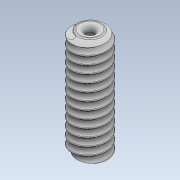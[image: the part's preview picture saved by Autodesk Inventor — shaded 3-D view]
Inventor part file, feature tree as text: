
AUTODESK INVENTOR PART (.ipt)
format: ipt  version: 2022 (Build 260153000, 153)  size: 748,032 bytes
history: native  units: in
note: dims shown in document units (in); Inventor stores cm internally (conversion verified against a paired STEP export)
features: sketch x7, revolve x4, extrude x3, fillet x3, thread x1, helix x1, other x1
ambient origin geometry x8: Origin, YZ Plane, XZ Plane, XY Plane, X Axis, Y Axis, Z Axis, Center Point
bodies: Solid1 (feature_tree), Solid6 (feature_tree), Solid8 (feature_tree)
feature tree (20):
  extrude  "ShaftLength"  Depth=0.3937in TaperAngle=0.0deg
  extrude  "cannulaHole"  Depth=0.3937in TaperAngle=0.0deg
  fillet  "topFillet"  Radius=0.3779in
  thread  "Thread5"  [1 undecoded]
  extrude  "Extrusion3"  Depth=0.0197in
  revolve  "Revolution11"  [1 undecoded]
  fillet  "bottomFillet"  Radius=0.3779in
  revolve  "Revolution15"  [1 undecoded]
  revolve  "Revolution16"  [1 undecoded]
  helix  "Coil7"  [1 undecoded]
  revolve  "Revolution14"  [1 undecoded]
  fillet  "Fillet4"  Radius=0.0276in
  other  "shaft diameter"
  sketch  "Sketch2"  dims[d0=0.124in d1=0.3937in d2=0.0in]
  sketch  "Sketch18"  dims[d3=0.0295in d4=0.3937in d5=0.0in d15=0.3779in d36=0.3779in]
  sketch  "Sketch19"  dims[d60=0.3779in d72=0.0197in]
  sketch  "Sketch23"  dims[d82=0.3779in d94=0.3661in d95=0.0in d103=0.3779in]
  sketch  "Sketch24"  dims[d115=0.3937in d116=0.0in d117=0.0276in]
  sketch  "Sketch25"  dims[d118=90.0deg d119=0.0787in d127=0.3779in]
  sketch  "Sketch26"  dims[d139=360.0deg d141=0.3779in d142=0.0044in d143=0.0044in d146=0.0276in d148=0.3779in d150=0.0in d151=0.0in d152=0.0276in d153=0.4213in d154=0.3937in d155=0.0in d156=0.0in d157=0.0in d158=0.0in d159=0.0in d160=0.0039in d120=0.0in d121=0.0in]
note: 6 required parameter values undecoded (feature->parameter linkage not recoverable at this tier; creation-order binding heuristic only, values carry confidence <= 0.55)